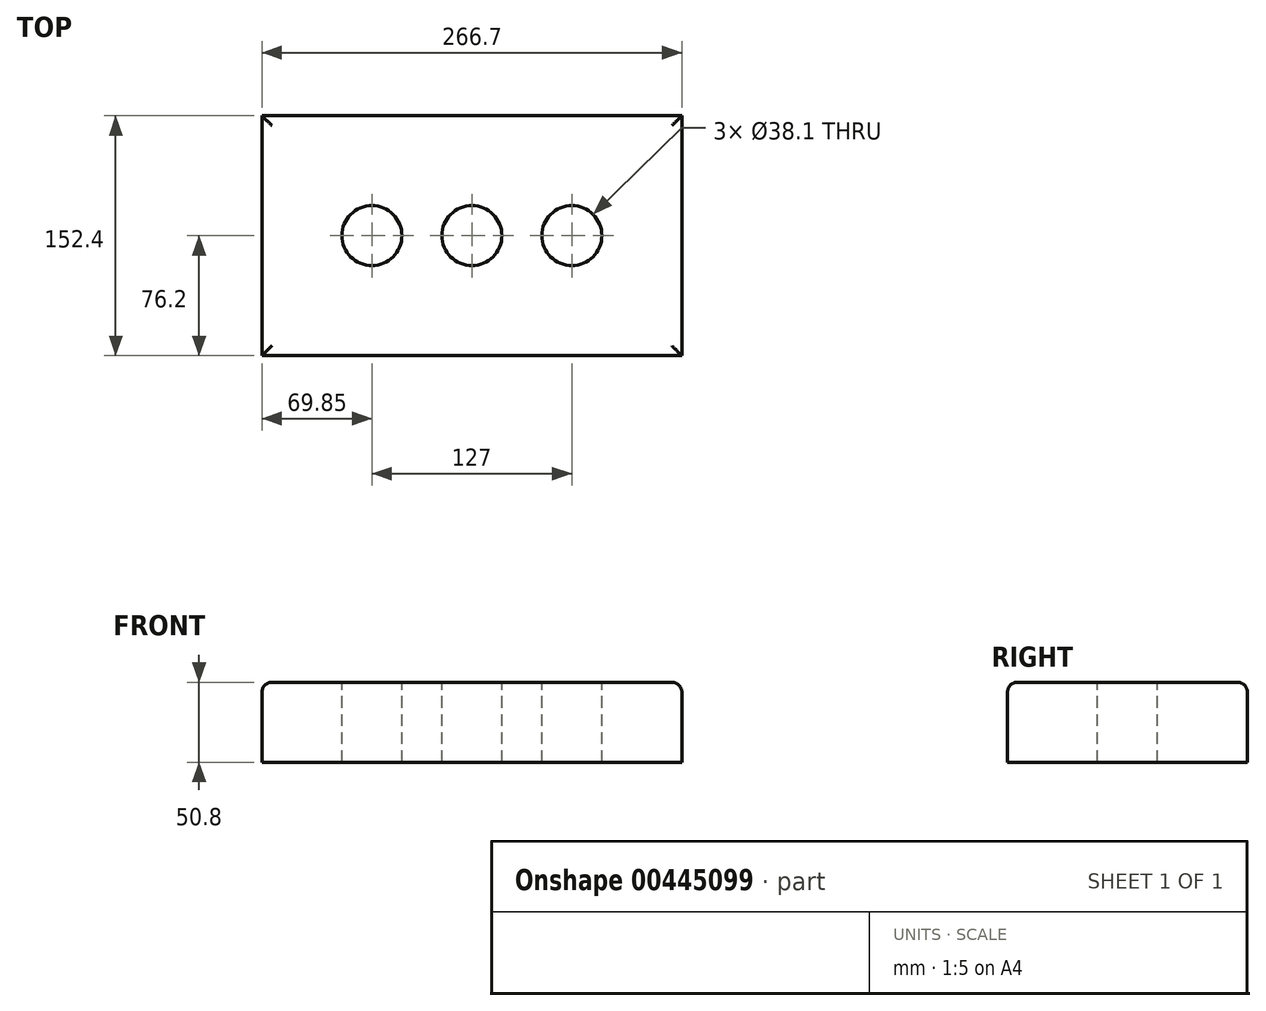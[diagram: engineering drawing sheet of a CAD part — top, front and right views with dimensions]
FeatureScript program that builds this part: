
annotation { "Feature Type Name" : "Feature", "Feature Type Description" : "" }
export const myFeature = defineFeature(function(context is Context, id is Id, definition is map)
    precondition{}
    {
        {
            var Q0;
            Q0=qCreatedBy(makeId("Top.planeOp"),FACE);
            var sketch = newSketch(context, id + "F0", { "sketchPlane" : qUnion([Q0])});
            skLineSegment(sketch, "E0.bottom", {"start": v(133.35, 76.2) * mm, "end": v(-133.35, 76.2) * mm});
            skLineSegment(sketch, "E0.top", {"start": v(133.35, -76.2) * mm, "end": v(-133.35, -76.2) * mm});
            skLineSegment(sketch, "E0.left", {"start": v(133.35, 76.2) * mm, "end": v(133.35, -76.2) * mm});
            skLineSegment(sketch, "E0.right", {"start": v(-133.35, 76.2) * mm, "end": v(-133.35, -76.2) * mm});
            skPoint(sketch, "E0.middle", {"position": v(0, 0) * mm});
            skCircle(sketch, "E1", {"center": v(0, 0) * mm, "radius": 19.05 * mm});
            skLineSegment(sketch, "E2", {"start": v(19.05, 0) * mm, "end": v(44.45, 0) * mm});
            skCircle(sketch, "E3", {"center": v(63.5, 0) * mm, "radius": 19.05 * mm});
            skLineSegment(sketch, "E4", {"start": v(-19.05, 0) * mm, "end": v(-44.45, 0) * mm});
            skCircle(sketch, "E5", {"center": v(-63.5, 0) * mm, "radius": 19.05 * mm});
            skSolve(sketch);
        }
        {
            var Q0;
            Q0 = qSketchRegion(id + "F0", true);
            extrude(context, id + "F1", {"entities" : qUnion([Q0]), "oppositeDirection" : true, "depth" : 50.8 * mm});
        }
        {
            var Q0;
            Q0=makeQuery(id+"F0.imprint","IMPRINT",FACE,{"disambiguationData":[TD([[makeQuery(id+"F0.imprint","IMPRINT",EDGE,{"derivedFrom":sQuery(id+"F0.wireOp",EDGE,"E3")}),1.0]])]});
            var Q1;
            {var subQ0=sQuery(id+"F0.wireOp",EDGE,"E1");var subQ1=makeQuery(id+"F0.imprint","IMPRINT",VERTEX,{"disambiguationData":[OD(0.0)],"derivedFrom":subQ0});Q1=makeQuery(id+"F0.imprint","IMPRINT",FACE,{"disambiguationData":[TD([[makeQuery(id+"F0.imprint","IMPRINT",EDGE,{"disambiguationData":[TD([[subQ1,-1.0]])],"derivedFrom":subQ0}),1.0]])]});}
            var Q2;
            Q2=makeQuery(id+"F0.imprint","IMPRINT",FACE,{"disambiguationData":[TD([[makeQuery(id+"F0.imprint","IMPRINT",EDGE,{"derivedFrom":sQuery(id+"F0.wireOp",EDGE,"E5")}),1.0]])]});
            extrude(context, id + "F2", {"entities" : qUnion([Q0, Q1, Q2]), "operationType" : NewBodyOperationType.REMOVE, "oppositeDirection" : true, "depth" : 50.8 * mm});
        }
        {
            var Q0;
            Q0=makeQuery(id+"F1.opExtrude","CAP_EDGE",EDGE,{"disambiguationData":[OSD([sQuery(id+"F0.wireOp",EDGE,"E0.bottom")])],"isStart":true});
            var Q1;
            Q1=makeQuery(id+"F1.opExtrude","CAP_EDGE",EDGE,{"disambiguationData":[OSD([sQuery(id+"F0.wireOp",EDGE,"E0.right")])],"isStart":true});
            var Q2;
            Q2=makeQuery(id+"F1.opExtrude","CAP_EDGE",EDGE,{"disambiguationData":[OSD([sQuery(id+"F0.wireOp",EDGE,"E0.left")])],"isStart":true});
            var Q3;
            Q3=makeQuery(id+"F1.opExtrude","CAP_EDGE",EDGE,{"disambiguationData":[OSD([sQuery(id+"F0.wireOp",EDGE,"E0.top")])],"isStart":true});
            fillet(context, id + "F3", {"entities" : qUnion([Q0, Q1, Q2, Q3]), "radius" : 6.35 * mm, "tangentPropagation" : true, "allowEdgeOverflow" : false});
        }
    });
